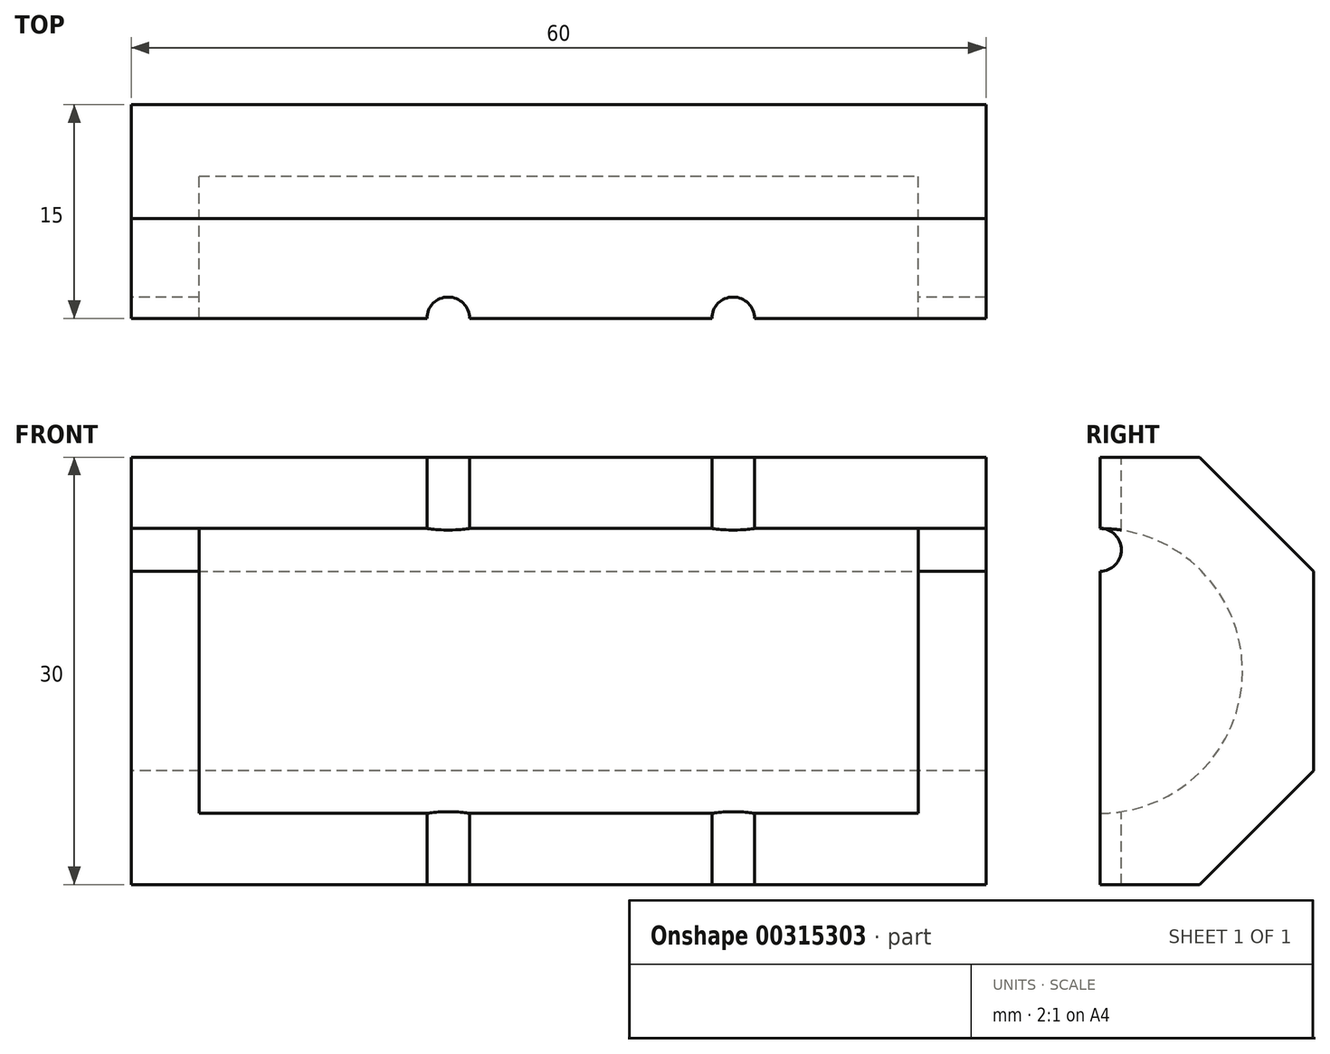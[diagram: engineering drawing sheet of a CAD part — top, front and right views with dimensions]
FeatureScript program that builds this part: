
annotation { "Feature Type Name" : "Feature", "Feature Type Description" : "" }
export const myFeature = defineFeature(function(context is Context, id is Id, definition is map)
    precondition{}
    {
        {
            var Q0;
            Q0=qCreatedBy(makeId("Front.planeOp"),FACE);
            var sketch = newSketch(context, id + "F0", { "sketchPlane" : qUnion([Q0])});
            skLineSegment(sketch, "E0.bottom", {"start": v(0, 15) * mm, "end": v(60, 15) * mm});
            skLineSegment(sketch, "E0.top", {"start": v(0, -15) * mm, "end": v(60, -15) * mm});
            skLineSegment(sketch, "E0.left", {"start": v(0, 15) * mm, "end": v(0, -15) * mm});
            skLineSegment(sketch, "E0.right", {"start": v(60, 15) * mm, "end": v(60, -15) * mm});
            skPoint(sketch, "E1", {"position": v(0, 0) * mm});
            skSolve(sketch);
        }
        {
            var Q0;
            Q0 = qSketchRegion(id + "F0", true);
            extrude(context, id + "F1", {"entities" : qUnion([Q0]), "oppositeDirection" : true, "depth" : 15 * mm});
        }
        {
            var Q0;
            Q0=qCreatedBy(makeId("Front.planeOp"),FACE);
            var sketch = newSketch(context, id + "F2", { "sketchPlane" : qUnion([Q0])});
            skLineSegment(sketch, "E2", {"start": v(0, 0) * mm, "end": v(60, 0) * mm, "construction": true});
            skLineSegment(sketch, "E3", {"start": v(0, 6.7) * mm, "end": v(60, 6.7) * mm, "construction": true});
            skLineSegment(sketch, "E4", {"start": v(0, 10) * mm, "end": v(60, 10) * mm, "construction": true});
            skLineSegment(sketch, "E5", {"start": v(0, 1.5) * mm, "end": v(60, 1.5) * mm, "construction": true});
            skSolve(sketch);
        }
        {
            var Q0;
            Q0=qCreatedBy(makeId("Front.planeOp"),FACE);
            var sketch = newSketch(context, id + "F3", { "sketchPlane" : qUnion([Q0])});
            skLineSegment(sketch, "E6.bottom", {"start": v(4.75, 10) * mm, "end": v(55.25, 10) * mm});
            skLineSegment(sketch, "E6.left", {"start": v(4.75, 10) * mm, "end": v(4.75, 0) * mm});
            skLineSegment(sketch, "E6.right", {"start": v(55.25, 0) * mm, "end": v(55.25, 10) * mm});
            skPoint(sketch, "E7", {"position": v(4.75, 0) * mm});
            skLineSegment(sketch, "E8", {"start": v(4.75, 0) * mm, "end": v(55.25, 0) * mm});
            skSolve(sketch);
        }
        {
            var Q0;
            Q0 = qSketchRegion(id + "F3", true);
            var Q1;
            Q1=sQuery(id+"F3.wireOp",EDGE,"E8");
            revolve(context, id + "F4", {"operationType" : NewBodyOperationType.REMOVE, "entities" : qUnion([Q0]), "axis" : qUnion([Q1]), "revolveType" : RevolveType.FULL, "oppositeDirection" : true});
        }
        {
            var Q0;
            Q0=qCreatedBy(makeId("Right.planeOp"),FACE);
            var sketch = newSketch(context, id + "F5", { "sketchPlane" : qUnion([Q0])});
            skCircle(sketch, "E9", {"center": v(0, 8.5) * mm, "radius": 1.5 * mm});
            skPoint(sketch, "E10", {"position": v(0, 10) * mm});
            skSolve(sketch);
        }
        {
            var Q0;
            Q0 = qSketchRegion(id + "F5", true);
            extrude(context, id + "F6", {"entities" : qUnion([Q0]), "operationType" : NewBodyOperationType.REMOVE, "endBound" : BoundingType.THROUGH_ALL, "depth" : 25 * mm});
        }
        {
            var Q0;
            Q0=qCreatedBy(makeId("Top.planeOp"),FACE);
            var sketch = newSketch(context, id + "F7", { "sketchPlane" : qUnion([Q0])});
            skCircle(sketch, "E11", {"center": v(22.25, 0) * mm, "radius": 1.5 * mm});
            skCircle(sketch, "E12", {"center": v(42.25, 0) * mm, "radius": 1.5 * mm});
            skSolve(sketch);
        }
        {
            var Q0;
            Q0 = qSketchRegion(id + "F7", true);
            extrude(context, id + "F8", {"entities" : qUnion([Q0]), "operationType" : NewBodyOperationType.REMOVE, "endBound" : BoundingType.THROUGH_ALL, "oppositeDirection" : true, "depth" : 25 * mm, "hasSecondDirection" : true, "secondDirectionBound" : SecondDirectionBoundingType.THROUGH_ALL, "secondDirectionOppositeDirection" : false, "secondDirectionDepth" : 25 * mm});
        }
        {
            var Q0;
            Q0=makeQuery(id+"F1.opExtrude","CAP_EDGE",EDGE,{"disambiguationData":[OSD([sQuery(id+"F0.wireOp",EDGE,"E0.bottom")])],"isStart":false});
            var Q1;
            Q1=makeQuery(id+"F1.opExtrude","CAP_EDGE",EDGE,{"disambiguationData":[OSD([sQuery(id+"F0.wireOp",EDGE,"E0.top")])],"isStart":false});
            chamfer(context, id + "F9", {"entities" : qUnion([Q0, Q1]), "width" : 8 * mm, "tangentPropagation" : true});
        }
    });
